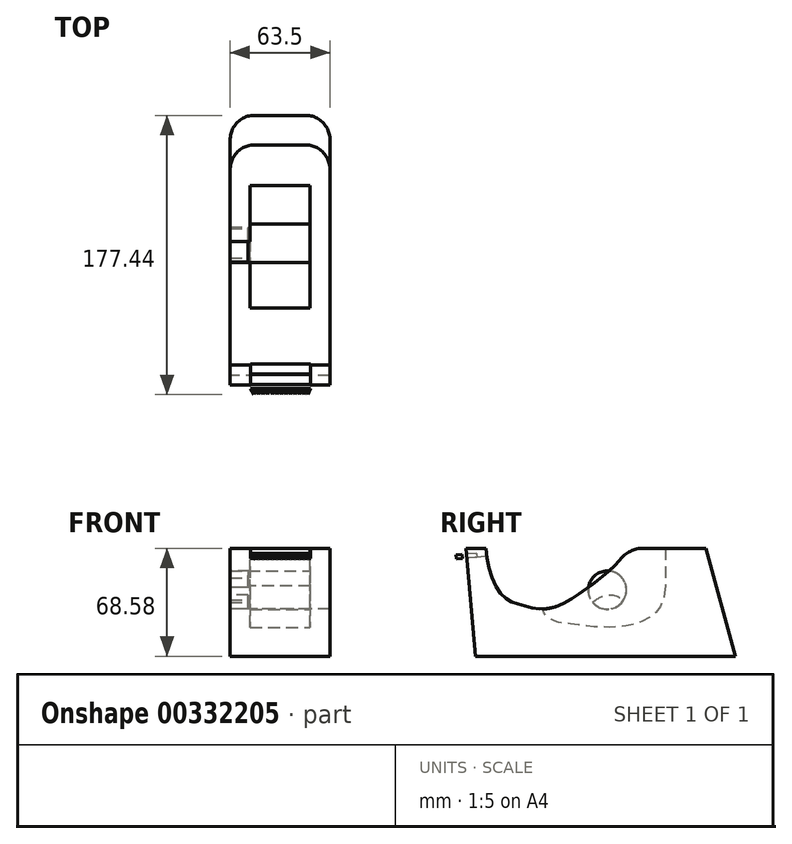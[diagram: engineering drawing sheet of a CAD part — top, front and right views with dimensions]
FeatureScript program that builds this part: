
annotation { "Feature Type Name" : "Feature", "Feature Type Description" : "" }
export const myFeature = defineFeature(function(context is Context, id is Id, definition is map)
    precondition{}
    {
        {
            var Q0;
            Q0=qCreatedBy(makeId("Right.planeOp"),FACE);
            var sketch = newSketch(context, id + "F0", { "sketchPlane" : qUnion([Q0])});
            skLineSegment(sketch, "E0", {"start": v(63.71, 34.3) * mm, "end": v(-88.69, 34.3) * mm});
            skLineSegment(sketch, "E1", {"start": v(63.71, 34.3) * mm, "end": v(82.55, -34.3) * mm});
            skLineSegment(sketch, "E2", {"start": v(82.55, -34.3) * mm, "end": v(-82.55, -34.3) * mm});
            skLineSegment(sketch, "E3", {"start": v(-82.55, -34.3) * mm, "end": v(-88.69, 34.3) * mm});
            skLineSegment(sketch, "E4", {"start": v(63.71, 34.3) * mm, "end": v(63.71, -34.3) * mm});
            skSolve(sketch);
        }
        {
            var Q0;
            Q0=makeQuery(id+"F0.imprint","IMPRINT",FACE,{"disambiguationData":[TD([[makeQuery(id+"F0.imprint","IMPRINT",EDGE,{"derivedFrom":sQuery(id+"F0.wireOp",EDGE,"E0")}),1.0]])]});
            var Q1;
            {var subQ0=sQuery(id+"F0.wireOp",EDGE,"E1");Q1=makeQuery(id+"F0.imprint","IMPRINT",FACE,{"disambiguationData":[TD([[makeQuery(id+"F0.imprint","IMPRINT",EDGE,{"derivedFrom":subQ0}),-1.0]])]});}
            extrude(context, id + "F1", {"entities" : qUnion([Q0, Q1]), "endBound" : BoundingType.SYMMETRIC, "depth" : 63.5 * mm});
        }
        {
            var Q0;
            Q0=makeQuery(id+"F1.opExtrude","CAP_EDGE",EDGE,{"disambiguationData":[OSD([sQuery(id+"F0.wireOp",EDGE,"E1")])],"isStart":true});
            var Q1;
            Q1=makeQuery(id+"F1.opExtrude","CAP_EDGE",EDGE,{"disambiguationData":[OSD([sQuery(id+"F0.wireOp",EDGE,"E1")])],"isStart":false});
            fillet(context, id + "F2", {"entities" : qUnion([Q0, Q1]), "radius" : 15.24 * mm, "tangentPropagation" : true, "allowEdgeOverflow" : false});
        }
        {
            var Q0;
            Q0=makeQuery(id+"F1.opExtrude","CAP_FACE",FACE,{"disambiguationData":[OSD([sQuery(id+"F0.wireOp",EDGE,"E0"),sQuery(id+"F0.wireOp",EDGE,"E1"),sQuery(id+"F0.wireOp",EDGE,"E2"),sQuery(id+"F0.wireOp",EDGE,"E3")])],"isStart":true});
            var sketch = newSketch(context, id + "F3", { "sketchPlane" : qUnion([Q0])});
            skFitSpline(sketch, "E5", {"points": [v(75.99, 34.3) * mm, v(66.78, 5.76) * mm, v(53.36, -1.87) * mm, v(35.12, -3.81) * mm, v(12.7, 8.07) * mm, v(-0.27, 18.06) * mm, v(-12.91, 34.3) * mm], "startDerivative": vector(-13.55, -142.95) * mm, "endDerivative": vector(-29.43, 118.32) * mm});
            skSolve(sketch);
        }
        {
            var Q0;
            {var subQ0=sQuery(id+"F3.wireOp",EDGE,"E5");Q0=makeQuery(id+"F3.imprint","IMPRINT",FACE,{"disambiguationData":[TD([[makeQuery(id+"F3.imprint","IMPRINT",EDGE,{"derivedFrom":subQ0}),-1.0]])]});}
            var Q1;
            Q1=sQuery(id+"F3.wireOp",EDGE,"E5");
            extrude(context, id + "F4", {"entities" : qUnion([Q0]), "operationType" : NewBodyOperationType.REMOVE, "surfaceEntities" : qUnion([Q1]), "oppositeDirection" : true, "depth" : 2540 * mm});
        }
        {
            var Q0;
            {var subQ0=sQuery(id+"F3.wireOp",EDGE,"E5");var subQ1=sQuery(id+"F0.wireOp",EDGE,"E0");Q0=makeQuery(id+"F4.boolean.opBoolean","COPY",EDGE,{"derivedFrom":makeQuery(id+"F4.opExtrude","SWEPT_EDGE",EDGE,{"disambiguationData":[OSD([subQ1,subQ0]),TDD([makeQuery(id+"F3.imprint","INTERSECT",VERTEX,{"disambiguationData":[OD(1.0)],"derivedFrom":[makeQuery(id+"F1.opExtrude","CAP_EDGE",EDGE,{"disambiguationData":[OSD([subQ1])],"isStart":true}),subQ0]})])]})});}
            fillet(context, id + "F5", {"entities" : qUnion([Q0]), "radius" : 19.05 * mm, "tangentPropagation" : true, "allowEdgeOverflow" : false});
        }
        {
            var Q0;
            Q0=qCreatedBy(makeId("Right.planeOp"),FACE);
            var sketch = newSketch(context, id + "F6", { "sketchPlane" : qUnion([Q0])});
            skLineSegment(sketch, "E6", {"start": v(38.1, 39.04) * mm, "end": v(38.1, 10.37) * mm});
            skFitSpline(sketch, "E7", {"points": [v(38.1, 10.37) * mm, v(35.2, -2.16) * mm, v(22.2, -12.76) * mm, v(4.12, -15.89) * mm, v(-11.54, -15.17) * mm, v(-26.72, -13.24) * mm, v(-32.26, -12.03) * mm, v(-34.9, -10.35) * mm, v(-37.8, -8.42) * mm, v(-39.25, -6.5) * mm, v(-40.45, 0) * mm], "startDerivative": vector(-8.6, -108.32) * mm, "endDerivative": vector(-11.12, 87.8) * mm});
            skFitSpline(sketch, "E8", {"points": [v(-40.45, 0) * mm, v(-36.11, 27.24) * mm, v(-22.14, 40.49) * mm, v(2.2, 44.83) * mm, v(26.53, 43.38) * mm, v(38.1, 39.04) * mm], "startDerivative": vector(5.97, 130.85) * mm, "endDerivative": vector(67.78, -32.38) * mm});
            skSolve(sketch);
        }
        {
            var Q0;
            Q0 = qSketchRegion(id + "F6", true);
            extrude(context, id + "F7", {"entities" : qUnion([Q0]), "operationType" : NewBodyOperationType.REMOVE, "endBound" : BoundingType.SYMMETRIC, "depth" : 38.2 * mm});
        }
        {
            var Q0;
            Q0=makeQuery(id+"F1.opExtrude","CAP_FACE",FACE,{"disambiguationData":[OSD([sQuery(id+"F0.wireOp",EDGE,"E0"),sQuery(id+"F0.wireOp",EDGE,"E1"),sQuery(id+"F0.wireOp",EDGE,"E2"),sQuery(id+"F0.wireOp",EDGE,"E3")])],"isStart":true});
            var sketch = newSketch(context, id + "F8", { "sketchPlane" : qUnion([Q0])});
            skCircle(sketch, "E9", {"center": v(-1.12, 7.8) * mm, "radius": 12.2 * mm});
            skPoint(sketch, "E9.first.point", {"position": v(-13.3, 8.4) * mm});
            skPoint(sketch, "E9.second.point", {"position": v(10.98, 9.3) * mm});
            skPoint(sketch, "E9.third.point", {"position": v(-1.09, -4.4) * mm});
            skSolve(sketch);
        }
        {
            var Q0;
            Q0 = qSketchRegion(id + "F8", true);
            extrude(context, id + "F9", {"entities" : qUnion([Q0]), "operationType" : NewBodyOperationType.REMOVE, "oppositeDirection" : true, "depth" : 40.64 * mm});
        }
        {
            var Q0;
            Q0=makeQuery(id+"F7.boolean.opBoolean","COPY",FACE,{"derivedFrom":makeQuery(id+"F7.opExtrude","CAP_FACE",FACE,{"disambiguationData":[OSD([sQuery(id+"F6.wireOp",EDGE,"E6"),sQuery(id+"F6.wireOp",EDGE,"E7"),sQuery(id+"F6.wireOp",EDGE,"E8")])],"isStart":false})});
            var sketch = newSketch(context, id + "F10", { "sketchPlane" : qUnion([Q0])});
            skCircle(sketch, "E10", {"center": v(-1.28, 7.67) * mm, "radius": 12.17 * mm});
            skPoint(sketch, "E10.first.point", {"position": v(-8.15, 17.71) * mm});
            skPoint(sketch, "E10.second.point", {"position": v(10.45, 4.43) * mm});
            skPoint(sketch, "E10.third.point", {"position": v(0, -4.43) * mm});
            skSolve(sketch);
        }
        {
            var Q0;
            {var subQ0=sQuery(id+"F10.wireOp",EDGE,"E10");var subQ1=makeQuery(id+"F7.boolean.opBoolean","INTERSECT",EDGE,{"derivedFrom":[makeQuery(id+"F4.boolean.opBoolean","COPY",FACE,{"derivedFrom":makeQuery(id+"F4.opExtrude","SWEPT_FACE",FACE,{"disambiguationData":[OSD([sQuery(id+"F3.wireOp",EDGE,"E5")])]})}),makeQuery(id+"F7.opExtrude","CAP_FACE",FACE,{"disambiguationData":[OSD([sQuery(id+"F6.wireOp",EDGE,"E6"),sQuery(id+"F6.wireOp",EDGE,"E7"),sQuery(id+"F6.wireOp",EDGE,"E8")])],"isStart":false})]});var subQ2=makeQuery(id+"F10.imprint","INTERSECT",VERTEX,{"disambiguationData":[OD(0.0)],"derivedFrom":[subQ1,subQ0]});Q0=makeQuery(id+"F10.imprint","IMPRINT",FACE,{"disambiguationData":[TD([[makeQuery(id+"F10.imprint","IMPRINT",EDGE,{"disambiguationData":[TD([[subQ2,1.0]])],"derivedFrom":subQ0}),1.0]])]});}
            var Q1;
            {var subQ0=sQuery(id+"F10.wireOp",EDGE,"E10");var subQ1=makeQuery(id+"F7.boolean.opBoolean","INTERSECT",EDGE,{"derivedFrom":[makeQuery(id+"F4.boolean.opBoolean","COPY",FACE,{"derivedFrom":makeQuery(id+"F4.opExtrude","SWEPT_FACE",FACE,{"disambiguationData":[OSD([sQuery(id+"F3.wireOp",EDGE,"E5")])]})}),makeQuery(id+"F7.opExtrude","CAP_FACE",FACE,{"disambiguationData":[OSD([sQuery(id+"F6.wireOp",EDGE,"E6"),sQuery(id+"F6.wireOp",EDGE,"E7"),sQuery(id+"F6.wireOp",EDGE,"E8")])],"isStart":false})]});var subQ2=makeQuery(id+"F10.imprint","INTERSECT",VERTEX,{"disambiguationData":[OD(0.0)],"derivedFrom":[subQ1,subQ0]});Q1=makeQuery(id+"F10.imprint","IMPRINT",FACE,{"disambiguationData":[TD([[makeQuery(id+"F10.imprint","IMPRINT",EDGE,{"disambiguationData":[TD([[subQ2,-1.0]])],"derivedFrom":subQ0}),1.0]])]});}
            extrude(context, id + "F11", {"entities" : qUnion([Q0, Q1]), "depth" : 39.37 * mm});
        }
        {
            var Q0;
            Q0=makeQuery(id+"F11.opExtrude","CAP_FACE",FACE,{"disambiguationData":[OSD([sQuery(id+"F10.wireOp",EDGE,"E10")])],"isStart":false});
            var sketch = newSketch(context, id + "F12", { "sketchPlane" : qUnion([Q0])});
            skLineSegment(sketch, "E11", {"start": v(-2.36, 19.8) * mm, "end": v(10.74, 9.55) * mm});
            skArc(sketch, "E12", {"start": v(8.17, 0) * mm, "mid": v(10.62, 4.46) * mm, "end": v(10.74, 9.55) * mm});
            skFitSpline(sketch, "E13", {"points": [v(8.17, 0) * mm, v(2.15, 3.59) * mm, v(-6.87, 4.01) * mm, v(-11.73, 1.44) * mm, v(-11.73, 1.43) * mm], "startDerivative": vector(-16.96, 12.38) * mm, "endDerivative": vector(0.8, -0.47) * mm});
            skArc(sketch, "E14", {"start": v(-2.36, 19.8) * mm, "mid": v(-12.1, 13.2) * mm, "end": v(-11.73, 1.43) * mm});
            skSolve(sketch);
        }
        {
            var Q0;
            {var subQ0=sQuery(id+"F12.wireOp",EDGE,"E11");Q0=makeQuery(id+"F12.imprint","IMPRINT",FACE,{"disambiguationData":[TD([[makeQuery(id+"F12.imprint","IMPRINT",EDGE,{"derivedFrom":subQ0}),-1.0]])]});}
            extrude(context, id + "F13", {"entities" : qUnion([Q0]), "operationType" : NewBodyOperationType.ADD, "depth" : 11.43 * mm});
        }
        {
            var Q0;
            Q0=makeQuery(id+"F1.opExtrude","SWEPT_FACE",FACE,{"disambiguationData":[OSD([sQuery(id+"F0.wireOp",EDGE,"E3")])]});
            var sketch = newSketch(context, id + "F14", { "sketchPlane" : qUnion([Q0])});
            skLineSegment(sketch, "E15", {"start": v(-18.73, 42.06) * mm, "end": v(-18.73, 35.71) * mm});
            skLineSegment(sketch, "E16", {"start": v(-18.73, 35.71) * mm, "end": v(19.21, 35.71) * mm});
            skLineSegment(sketch, "E17", {"start": v(19.21, 35.71) * mm, "end": v(19.21, 42.06) * mm});
            skSolve(sketch);
        }
        {
            var Q0;
            Q0 = qSketchRegion(id + "F14", true);
            var Q1;
            {var subQ0=sQuery(id+"F14.wireOp",EDGE,"E15");Q1=makeQuery(id+"F14.imprint","IMPRINT",FACE,{"disambiguationData":[TD([[makeQuery(id+"F14.imprint","IMPRINT",EDGE,{"derivedFrom":subQ0}),1.0]])]});}
            extrude(context, id + "F15", {"entities" : qUnion([Q0, Q1]), "operationType" : NewBodyOperationType.REMOVE, "oppositeDirection" : true, "depth" : 101.6 * mm});
        }
        {
            var Q0;
            Q0=makeQuery(id+"F15.boolean.opBoolean","COPY",FACE,{"derivedFrom":makeQuery(id+"F15.opExtrude","SWEPT_FACE",FACE,{"disambiguationData":[OSD([sQuery(id+"F14.wireOp",EDGE,"E16")])]})});
            var sketch = newSketch(context, id + "F16", { "sketchPlane" : qUnion([Q0])});
            skLineSegment(sketch, "E18.bottom", {"start": v(19.21, -78.85) * mm, "end": v(-18.73, -78.85) * mm});
            skLineSegment(sketch, "E18.top", {"start": v(19.21, -87.97) * mm, "end": v(-18.73, -87.97) * mm});
            skLineSegment(sketch, "E18.left", {"start": v(19.21, -78.85) * mm, "end": v(19.21, -87.97) * mm});
            skLineSegment(sketch, "E18.right", {"start": v(-18.73, -78.85) * mm, "end": v(-18.73, -87.97) * mm});
            skLineSegment(sketch, "E19", {"start": v(19.21, -87.97) * mm, "end": v(17.84, -91.85) * mm});
            skLineSegment(sketch, "E20", {"start": v(17.84, -91.85) * mm, "end": v(16.55, -87.97) * mm});
            skLineSegment(sketch, "E21", {"start": v(16.55, -87.97) * mm, "end": v(15.18, -91.85) * mm});
            skLineSegment(sketch, "E22", {"start": v(15.18, -91.85) * mm, "end": v(13.82, -87.97) * mm});
            skLineSegment(sketch, "E23", {"start": v(13.82, -87.97) * mm, "end": v(12.45, -91.85) * mm});
            skLineSegment(sketch, "E24", {"start": v(12.45, -91.85) * mm, "end": v(10.92, -87.97) * mm});
            skLineSegment(sketch, "E25", {"start": v(10.92, -87.97) * mm, "end": v(9.55, -91.85) * mm});
            skLineSegment(sketch, "E26", {"start": v(9.55, -91.85) * mm, "end": v(8.03, -87.97) * mm});
            skLineSegment(sketch, "E27", {"start": v(8.03, -87.97) * mm, "end": v(6.66, -91.85) * mm});
            skLineSegment(sketch, "E28", {"start": v(6.66, -91.85) * mm, "end": v(5.13, -87.97) * mm});
            skLineSegment(sketch, "E29", {"start": v(5.13, -87.97) * mm, "end": v(3.76, -91.85) * mm});
            skLineSegment(sketch, "E30", {"start": v(3.76, -91.85) * mm, "end": v(2.23, -87.97) * mm});
            skLineSegment(sketch, "E31", {"start": v(2.23, -87.97) * mm, "end": v(0.86, -91.85) * mm});
            skLineSegment(sketch, "E32", {"start": v(0.86, -91.85) * mm, "end": v(-0.66, -87.97) * mm});
            skLineSegment(sketch, "E33", {"start": v(-0.66, -87.97) * mm, "end": v(-2.03, -91.85) * mm});
            skLineSegment(sketch, "E34", {"start": v(-2.03, -91.85) * mm, "end": v(-3.56, -87.97) * mm});
            skLineSegment(sketch, "E35", {"start": v(-3.56, -87.97) * mm, "end": v(-4.93, -91.85) * mm});
            skLineSegment(sketch, "E36", {"start": v(-4.93, -91.85) * mm, "end": v(-6.46, -87.97) * mm});
            skLineSegment(sketch, "E37", {"start": v(-6.46, -87.97) * mm, "end": v(-7.83, -91.85) * mm});
            skLineSegment(sketch, "E38", {"start": v(-7.83, -91.85) * mm, "end": v(-9.35, -87.97) * mm});
            skLineSegment(sketch, "E39", {"start": v(-9.35, -87.97) * mm, "end": v(-10.72, -91.85) * mm});
            skLineSegment(sketch, "E40", {"start": v(-10.72, -91.85) * mm, "end": v(-12.25, -87.97) * mm});
            skLineSegment(sketch, "E41", {"start": v(-12.25, -87.97) * mm, "end": v(-13.62, -91.85) * mm});
            skLineSegment(sketch, "E42", {"start": v(-13.62, -91.85) * mm, "end": v(-15.15, -87.97) * mm});
            skLineSegment(sketch, "E43", {"start": v(-15.15, -87.97) * mm, "end": v(-16.52, -91.85) * mm});
            skLineSegment(sketch, "E44", {"start": v(-16.52, -91.85) * mm, "end": v(-18.73, -87.97) * mm});
            skSolve(sketch);
        }
        {
            var Q0;
            {var subQ17=makeQuery(id+"F15.boolean.opBoolean","COPY",EDGE,{"derivedFrom":makeQuery(id+"F15.opExtrude","CAP_EDGE",EDGE,{"disambiguationData":[OSD([sQuery(id+"F14.wireOp",EDGE,"E16")])],"isStart":true})});Q0=makeQuery(id+"F16.imprint","IMPRINT",FACE,{"disambiguationData":[TD([[makeQuery(id+"F16.imprint","IMPRINT",EDGE,{"derivedFrom":subQ17}),-1.0]])]});}
            var Q1;
            {var subQ0=sQuery(id+"F16.wireOp",EDGE,"E18.bottom");Q1=makeQuery(id+"F16.imprint","IMPRINT",FACE,{"disambiguationData":[TD([[makeQuery(id+"F16.imprint","IMPRINT",EDGE,{"derivedFrom":subQ0}),1.0]])]});}
            var Q2;
            {var subQ2=sQuery(id+"F16.wireOp",EDGE,"E43");Q2=makeQuery(id+"F16.imprint","IMPRINT",FACE,{"disambiguationData":[TD([[makeQuery(id+"F16.imprint","IMPRINT",EDGE,{"derivedFrom":subQ2}),-1.0]])]});}
            var Q3;
            {var subQ0=sQuery(id+"F16.wireOp",EDGE,"E41");Q3=makeQuery(id+"F16.imprint","IMPRINT",FACE,{"disambiguationData":[TD([[makeQuery(id+"F16.imprint","IMPRINT",EDGE,{"derivedFrom":subQ0}),-1.0]])]});}
            var Q4;
            {var subQ0=sQuery(id+"F16.wireOp",EDGE,"E39");Q4=makeQuery(id+"F16.imprint","IMPRINT",FACE,{"disambiguationData":[TD([[makeQuery(id+"F16.imprint","IMPRINT",EDGE,{"derivedFrom":subQ0}),-1.0]])]});}
            var Q5;
            {var subQ0=sQuery(id+"F16.wireOp",EDGE,"E37");Q5=makeQuery(id+"F16.imprint","IMPRINT",FACE,{"disambiguationData":[TD([[makeQuery(id+"F16.imprint","IMPRINT",EDGE,{"derivedFrom":subQ0}),-1.0]])]});}
            var Q6;
            {var subQ0=sQuery(id+"F16.wireOp",EDGE,"E35");Q6=makeQuery(id+"F16.imprint","IMPRINT",FACE,{"disambiguationData":[TD([[makeQuery(id+"F16.imprint","IMPRINT",EDGE,{"derivedFrom":subQ0}),-1.0]])]});}
            var Q7;
            {var subQ0=sQuery(id+"F16.wireOp",EDGE,"E33");Q7=makeQuery(id+"F16.imprint","IMPRINT",FACE,{"disambiguationData":[TD([[makeQuery(id+"F16.imprint","IMPRINT",EDGE,{"derivedFrom":subQ0}),-1.0]])]});}
            var Q8;
            {var subQ0=sQuery(id+"F16.wireOp",EDGE,"E29");Q8=makeQuery(id+"F16.imprint","IMPRINT",FACE,{"disambiguationData":[TD([[makeQuery(id+"F16.imprint","IMPRINT",EDGE,{"derivedFrom":subQ0}),-1.0]])]});}
            var Q9;
            {var subQ0=sQuery(id+"F16.wireOp",EDGE,"E31");Q9=makeQuery(id+"F16.imprint","IMPRINT",FACE,{"disambiguationData":[TD([[makeQuery(id+"F16.imprint","IMPRINT",EDGE,{"derivedFrom":subQ0}),-1.0]])]});}
            var Q10;
            {var subQ0=sQuery(id+"F16.wireOp",EDGE,"E27");Q10=makeQuery(id+"F16.imprint","IMPRINT",FACE,{"disambiguationData":[TD([[makeQuery(id+"F16.imprint","IMPRINT",EDGE,{"derivedFrom":subQ0}),-1.0]])]});}
            var Q11;
            {var subQ0=sQuery(id+"F16.wireOp",EDGE,"E25");Q11=makeQuery(id+"F16.imprint","IMPRINT",FACE,{"disambiguationData":[TD([[makeQuery(id+"F16.imprint","IMPRINT",EDGE,{"derivedFrom":subQ0}),-1.0]])]});}
            var Q12;
            {var subQ0=sQuery(id+"F16.wireOp",EDGE,"E23");Q12=makeQuery(id+"F16.imprint","IMPRINT",FACE,{"disambiguationData":[TD([[makeQuery(id+"F16.imprint","IMPRINT",EDGE,{"derivedFrom":subQ0}),-1.0]])]});}
            var Q13;
            {var subQ0=sQuery(id+"F16.wireOp",EDGE,"E21");Q13=makeQuery(id+"F16.imprint","IMPRINT",FACE,{"disambiguationData":[TD([[makeQuery(id+"F16.imprint","IMPRINT",EDGE,{"derivedFrom":subQ0}),-1.0]])]});}
            var Q14;
            {var subQ0=sQuery(id+"F16.wireOp",EDGE,"E19");Q14=makeQuery(id+"F16.imprint","IMPRINT",FACE,{"disambiguationData":[TD([[makeQuery(id+"F16.imprint","IMPRINT",EDGE,{"derivedFrom":subQ0}),-1.0]])]});}
            extrude(context, id + "F17", {"entities" : qUnion([Q0, Q1, Q2, Q3, Q4, Q5, Q6, Q7, Q8, Q9, Q10, Q11, Q12, Q13, Q14]), "oppositeDirection" : true, "depth" : -2.54 * mm});
        }
    });
